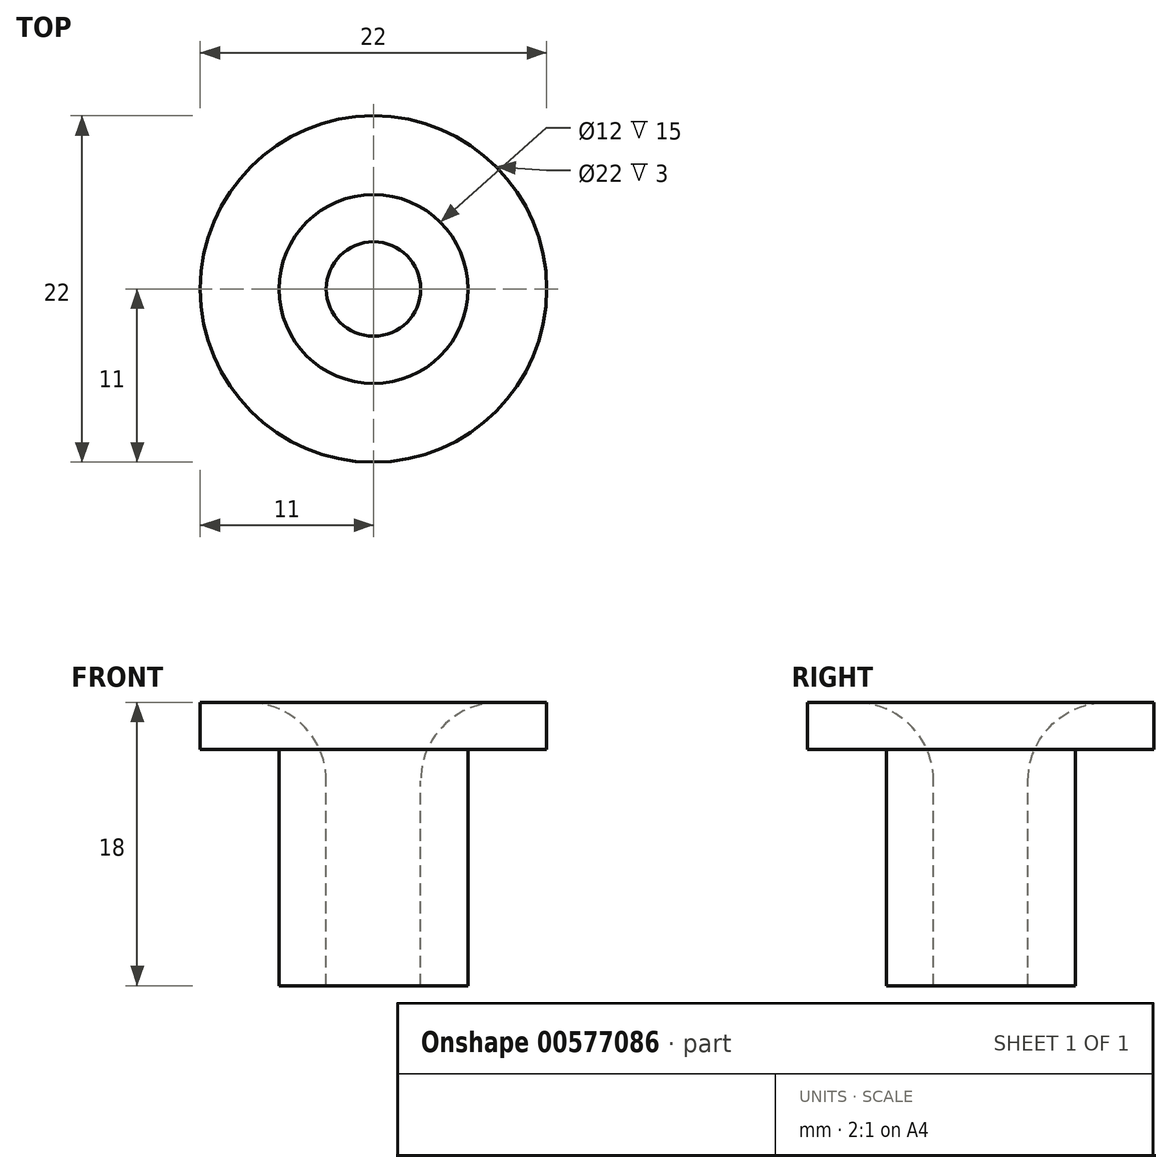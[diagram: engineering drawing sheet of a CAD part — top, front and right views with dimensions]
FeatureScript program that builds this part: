
annotation { "Feature Type Name" : "Feature", "Feature Type Description" : "" }
export const myFeature = defineFeature(function(context is Context, id is Id, definition is map)
    precondition{}
    {
        {
            var Q0;
            Q0=qCreatedBy(makeId("Front.planeOp"),FACE);
            var sketch = newSketch(context, id + "F0", { "sketchPlane" : qUnion([Q0])});
            skLineSegment(sketch, "E0", {"start": v(-6, 0) * mm, "end": v(-6, 15) * mm});
            skLineSegment(sketch, "E1", {"start": v(-6, 15) * mm, "end": v(-11, 15) * mm});
            skLineSegment(sketch, "E2", {"start": v(-11, 15) * mm, "end": v(-11, 18) * mm});
            skLineSegment(sketch, "E3", {"start": v(-11, 18) * mm, "end": v(-8, 18) * mm});
            skLineSegment(sketch, "E4", {"start": v(-3, 13) * mm, "end": v(-3, 0) * mm});
            skLineSegment(sketch, "E5", {"start": v(-3, 0) * mm, "end": v(-6, 0) * mm});
            skPoint(sketch, "E6.visualSharp", {"position": v(-3, 18) * mm});
            skArc(sketch, "E6.filletArc", {"start": v(-3, 13) * mm, "mid": v(-4.46, 16.54) * mm, "end": v(-8, 18) * mm});
            skLineSegment(sketch, "E7", {"start": v(0, 0) * mm, "end": v(0, 28.86) * mm, "construction": true});
            skSolve(sketch);
        }
        {
            var Q0;
            Q0=sQuery(id+"F0.wireOp",EDGE,"E2");
            var Q1;
            Q1=sQuery(id+"F0.wireOp",EDGE,"E3");
            var Q2;
            Q2=sQuery(id+"F0.wireOp",EDGE,"E6.filletArc");
            var Q3;
            Q3=sQuery(id+"F0.wireOp",EDGE,"E4");
            var Q4;
            Q4=sQuery(id+"F0.wireOp",EDGE,"E5");
            var Q5;
            Q5=sQuery(id+"F0.wireOp",EDGE,"E0");
            var Q6;
            Q6=sQuery(id+"F0.wireOp",EDGE,"E1");
            var Q7;
            Q7=sQuery(id+"F0.wireOp",EDGE,"E7");
            revolve(context, id + "F1", {"bodyType" : ToolBodyType.SURFACE, "surfaceEntities" : qUnion([Q0, Q1, Q2, Q3, Q4, Q5, Q6]), "axis" : qUnion([Q7]), "revolveType" : RevolveType.FULL});
        }
    });
